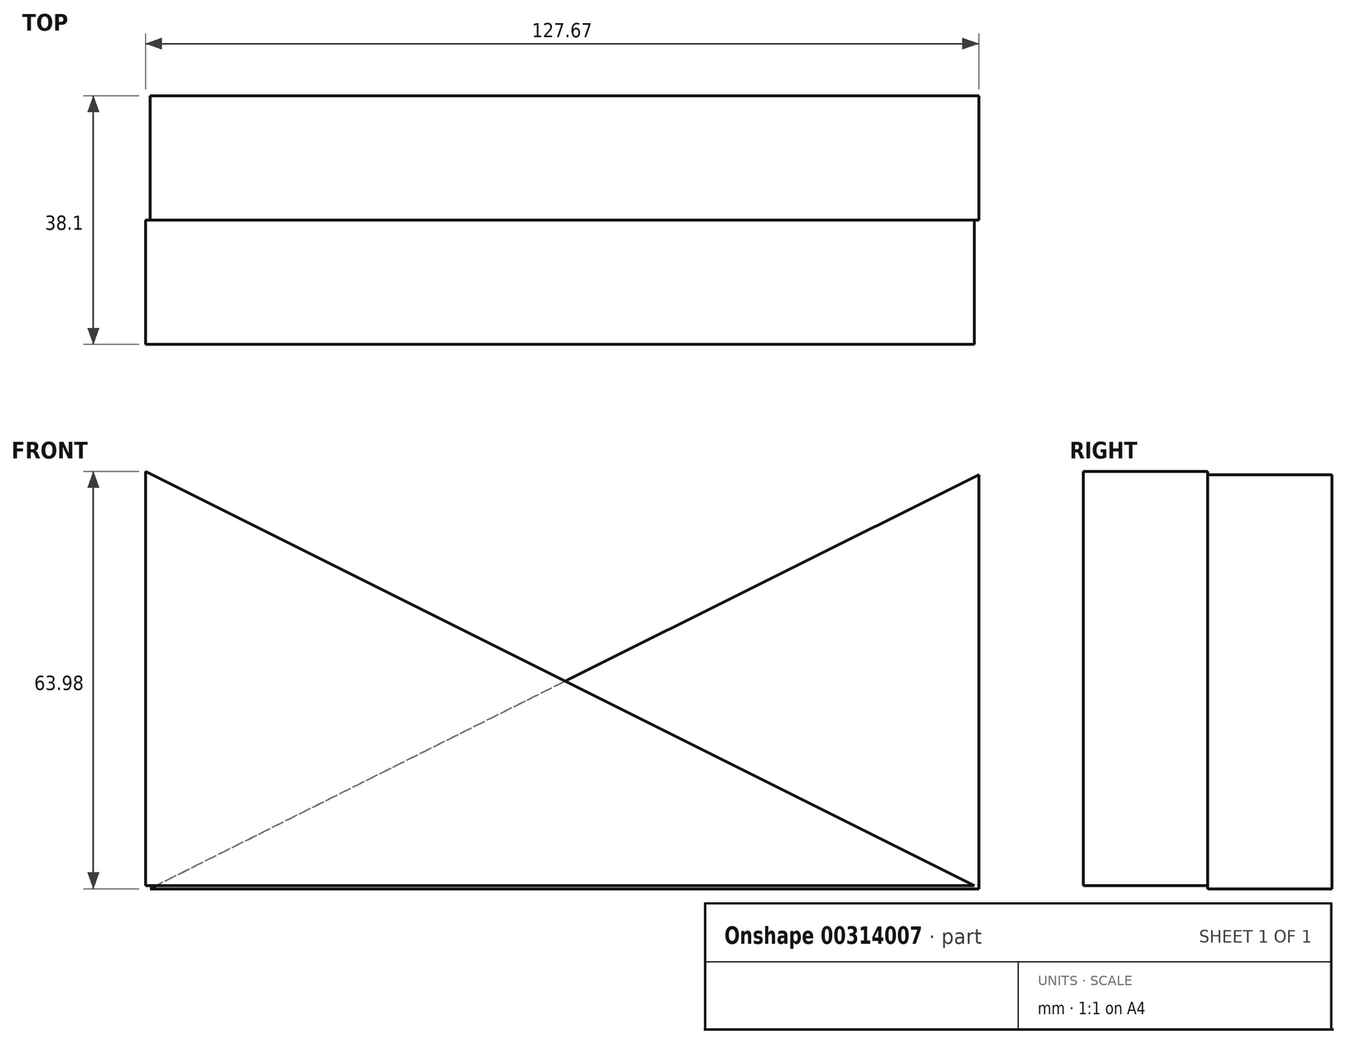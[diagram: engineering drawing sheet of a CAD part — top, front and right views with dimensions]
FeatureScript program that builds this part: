
annotation { "Feature Type Name" : "Feature", "Feature Type Description" : "" }
export const myFeature = defineFeature(function(context is Context, id is Id, definition is map)
    precondition{}
    {
        {
            var Q0;
            Q0=qCreatedBy(makeId("Front.planeOp"),FACE);
            var sketch = newSketch(context, id + "F0", { "sketchPlane" : qUnion([Q0])});
            skLineSegment(sketch, "E0", {"start": v(-36.12, 26.5) * mm, "end": v(-36.12, -37) * mm});
            skLineSegment(sketch, "E1", {"start": v(-36.12, -37) * mm, "end": v(90.88, -37) * mm});
            skLineSegment(sketch, "E2", {"start": v(-36.12, 26.5) * mm, "end": v(90.88, -37) * mm});
            skSolve(sketch);
        }
        {
            var Q0;
            Q0 = qSketchRegion(id + "F0", true);
            extrude(context, id + "F1", {"entities" : qUnion([Q0]), "depth" : 19.05 * mm});
        }
        {
            var Q0;
            Q0=qCreatedBy(makeId("Front.planeOp"),FACE);
            var sketch = newSketch(context, id + "F2", { "sketchPlane" : qUnion([Q0])});
            skLineSegment(sketch, "E3", {"start": v(-35.45, -37.48) * mm, "end": v(91.55, -37.48) * mm});
            skLineSegment(sketch, "E4", {"start": v(91.55, -37.48) * mm, "end": v(91.55, 26.02) * mm});
            skLineSegment(sketch, "E5", {"start": v(91.55, 26.02) * mm, "end": v(-35.45, -37.48) * mm});
            skSolve(sketch);
        }
        {
            var Q0;
            Q0=makeQuery(id+"F2.imprint","IMPRINT",FACE,{"disambiguationData":[TD([[makeQuery(id+"F2.imprint","IMPRINT",EDGE,{"derivedFrom":sQuery(id+"F2.wireOp",EDGE,"E3")}),1.0]])]});
            extrude(context, id + "F3", {"entities" : qUnion([Q0]), "operationType" : NewBodyOperationType.ADD, "oppositeDirection" : true, "depth" : 19.05 * mm});
        }
    });
